# Revit family: 4054980 Lighting Fixture_Sylvania_Brio IP65VR LED_Wall Surface
name_source: partatom
category: Lighting Fixtures
revit_build: Autodesk Revit 2017 (Build: 20190507_1515(x64)
units: mm (PartAtom-declared; Revit-internal decimal feet)

## family parameters
Cut with Voids When Loaded = No
Host = Face
Light Source = Yes
OmniClass Number = 23.80.70.11.17
OmniClass Title = Specialized Lighting by Location or Use
Part Type = Normal
Room Calculation Point = No
Round Connector Dimension = Use Diameter
Shared = No

## types (1)
- BRIO IP65VR LED 4000K
    Apparent Load = 22 VA
    Assembly Code = D5020200
    Body Material = Aluminum_Sylvania_Brio IP65 LED_Black
    Color Filter = 16777215
    Default Elevation = 0 mm  [stored 0 ft]
    Description = Significant energy savings compared to traditional CFL and 2D fixtures. Excellent flashing provides perfect homogenous light distribution. Unique feature allowing a choice between High Output or High efficiency with the flick of a switch. 50,000 hours life, providing a maintenance free lighting solution. Attractive, tough IK10 impact resistant construction. 104-119mm discrete profile. Aesthetically pleasing designs. IP65 water jet proof. Option to add microwave sensor for maximum energy savings
    Diffuser Material = Polycarbonate_Sylvania_Brio IP65 LED_Opal
    Dimming Lamp Color Temperature Shift = <None>
    Drive Current = 350mA or 700mA
    IK Rating = IK10
    IP Rating = IP65
    LOR = 44 %
    Lamp = Brio LED 4000K
    Lamp Comments = Integrated LED
    Length = 395 mm
    Life = 50 000h
    Manufacturer = Feilo-Sylvania Group
    Model = 4054956 BRIO IP65VR LED 4000K
    Photometric Web File = 4054956_BRIOIP65LED4000K700mABlack-131366.ies
    Product Family = BRIO IP65 Vandal Resistant LED
    Product Page URL = https://www.sylvania-lighting.com
    Tilt Angle = -90.00°
    URL = https://www.sylvania-lighting.com
    Voltage = 230 V
    Voltage Comments = UNV (Universal Voltage; 220-240 Volt)
    Weight = 3.00 kg
    Width = 350 mm  [stored 1.14829 ft]

note: [stored X ft] marks values corroborated as IEEE doubles in the binary element streams (Revit-internal decimal feet)

## geometry (parser evidence)
native form markers: Sweep x3
no freeform markers — native parametric forms only
